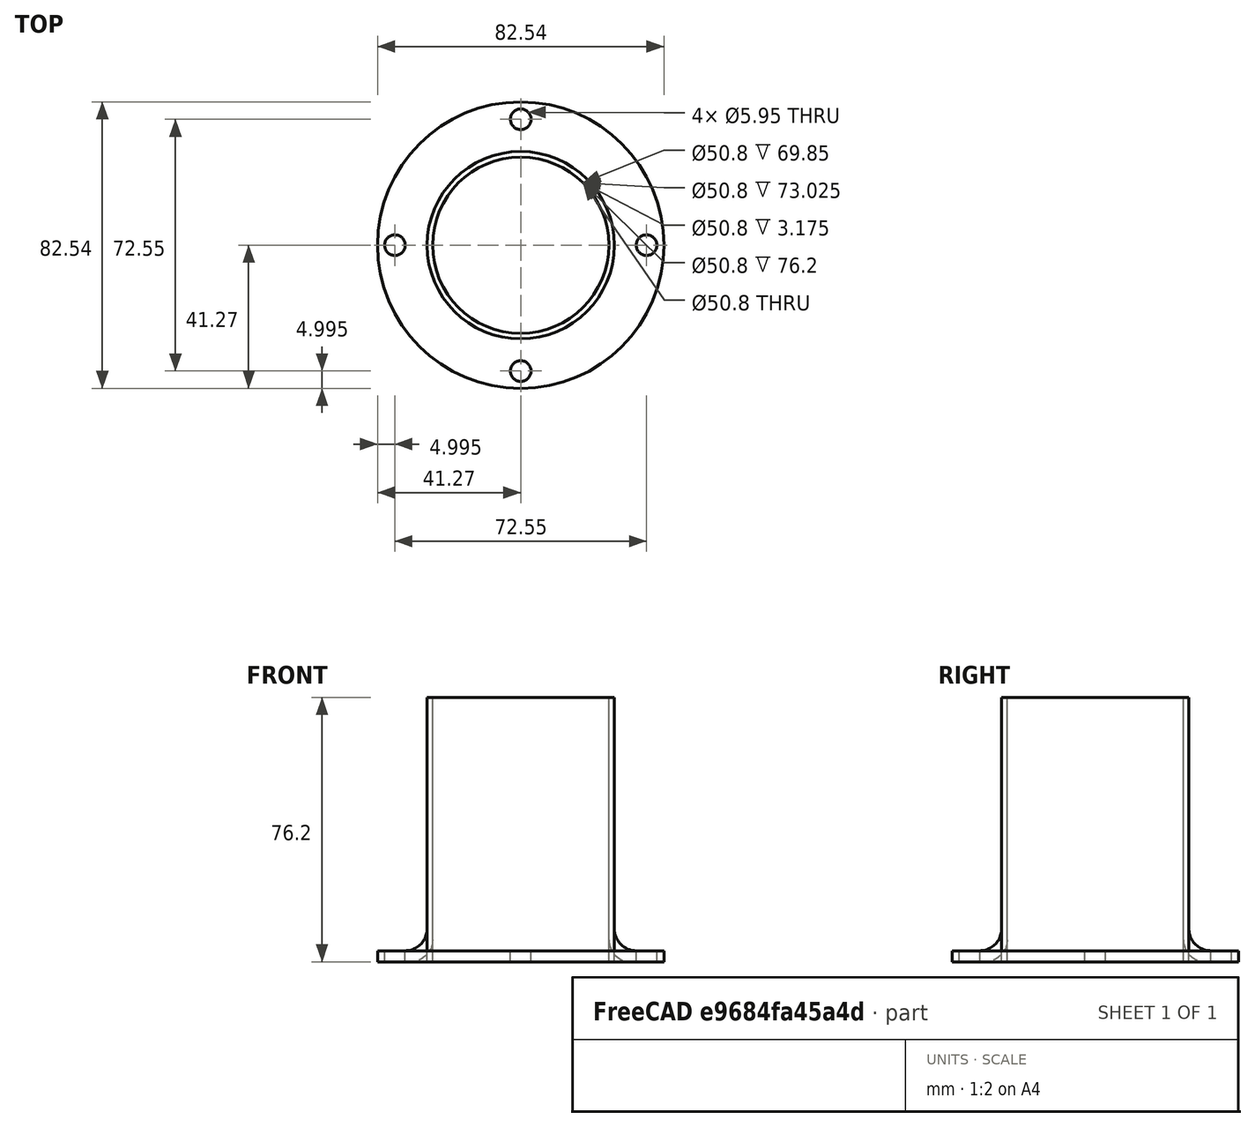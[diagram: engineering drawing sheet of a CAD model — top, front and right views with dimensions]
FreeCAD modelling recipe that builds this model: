
FCSTD DOCUMENT  (FreeCAD 0.22R38385 (Git))
Label: 2x3 Speaker Port
License: All rights reserved
objects: Part::FeaturePython×4, PartDesign::Fillet×2, Part::Fuse×1, Spreadsheet::Sheet×1, Mesh::Feature×1, PartDesign::Boolean×1, Sketcher::SketchObject×1, PartDesign::Hole×1, PartDesign::Body×1
note: 19 computed .brp shape members not serialized (recipe doc carries the construction recipe); baked Part::Feature solids carry a one-line shape summary decoded from their .brp

FEATURE [Part::FeaturePython] Tube  # WARN: FeaturePython — macro-defined, semantics opaque (R4)
  AttacherType = Attacher::AttachEngine3D
  Height = 76.2
  InnerRadius = 25.4
  OuterRadius = 26.9875
  expr: Height = Spreadsheet.port_length
  expr: InnerRadius = Spreadsheet.inner_radius
  expr: OuterRadius = Spreadsheet.outer_radius
FEATURE [Part::FeaturePython] Tube001  # WARN: FeaturePython — macro-defined, semantics opaque (R4)
  AttacherType = Attacher::AttachEngine3D
  Height = 3.175
  InnerRadius = 25.4
  OuterRadius = 41.275
  expr: Height = Spreadsheet.flange_thickness
  expr: InnerRadius = Spreadsheet.inner_radius
  expr: OuterRadius = Spreadsheet.flange_radius
FEATURE [Part::Fuse] Fusion
  Base = -> Tube
  Tool = -> Tube001
FEATURE [Spreadsheet::Sheet] Spreadsheet
  cells = A1='port_diameter; B1(port_diameter)==2 "; A2='port_length; B2(port_length)==3 "; A3='wall_thickness; B3(wall_thickness)==0.0625 "; A4='flange_diameter; B4(flange_diameter)==3.25 "; A5='flange_fillet; B5(flange_fillet)==0.25 "; A6='flange_thickness; B6(flange_thickness)==0.125 "; A7='screw_diameter; B7(screw_diameter)==5 mm; A9='computed values; A10='inner_radius; B10(inner_radius)==port_diameter / 2; A11='outer_radius; B11(outer_radius)==wall_thickness + inner_radius; A12='flange_radius; B12(flange_radius)==flange_diameter / 2; A13='screw_radius; B13(screw_radius)==2.5 mm
FEATURE [Mesh::Feature] Mesh  label="Body (Meshed)"
FEATURE [Part::FeaturePython] Tube002  # WARN: FeaturePython — macro-defined, semantics opaque (R4)
  AttacherType = Attacher::AttachEngine3D
  Height = 76.2
  InnerRadius = 25.4
  OuterRadius = 26.9875
  expr: .Placement.Base.z = 0
  expr: Height = Spreadsheet.port_length
  expr: InnerRadius = Spreadsheet.inner_radius
  expr: OuterRadius = Spreadsheet.outer_radius
FEATURE [Part::FeaturePython] Tube003  # WARN: FeaturePython — macro-defined, semantics opaque (R4)
  AttacherType = Attacher::AttachEngine3D
  Height = 3.175
  InnerRadius = 25.4
  OuterRadius = 41.275
  expr: Height = Spreadsheet.flange_thickness
  expr: InnerRadius = Spreadsheet.inner_radius
  expr: OuterRadius = Spreadsheet.flange_radius
FEATURE [PartDesign::Boolean] Boolean
  Group = -> [Tube003,Tube002]
  Refine = true
  Suppressed = false
  Type = 0
  UsePlacement = true
FEATURE [PartDesign::Fillet] Fillet
  Base = -> Boolean [Edge8]
  BaseFeature = -> Boolean
  Radius = 6.35
  SupportTransform = false
  Suppressed = false
  UseAllEdges = false
  expr: Radius = Spreadsheet.flange_fillet
FEATURE [PartDesign::Fillet] Fillet001
  Base = -> Fillet [Edge9]
  BaseFeature = -> Fillet
  Radius = 6.35
  SupportTransform = false
  Suppressed = false
  UseAllEdges = false
  expr: Radius = Spreadsheet.flange_fillet
FEATURE [Sketcher::SketchObject] Sketch
  ArcFitTolerance = 0
  AttachmentSupport = -> [Fillet001]
  FullyConstrained = true
  MakeInternals = false
  MapMode = 5
  Placement = pos=(0,0,0) rot=(1,0,0;3.14159rad)
  expr: Constraints[10] = Spreadsheet.flange_radius - Spreadsheet.screw_diameter
  expr: Constraints[11] = Spreadsheet.flange_radius - Spreadsheet.screw_diameter
  expr: Constraints[1] = Spreadsheet.flange_radius - Spreadsheet.screw_diameter
  expr: Constraints[2] = Spreadsheet.screw_radius
  expr: Constraints[6] = Spreadsheet.screw_radius
  expr: Constraints[7] = Spreadsheet.screw_radius
  expr: Constraints[8] = Spreadsheet.screw_radius
  expr: Constraints[9] = Spreadsheet.flange_radius - Spreadsheet.screw_diameter
  sketch-geometry (4):
    g0: Circle CenterX=0 CenterY=36.275 CenterZ=0 NormalX=0 NormalY=0 NormalZ=1 AngleXU=0 Radius=2.5
    g1: Circle CenterX=36.275 CenterY=0 CenterZ=0 NormalX=0 NormalY=0 NormalZ=1 AngleXU=0 Radius=2.5
    g2: Circle CenterX=0 CenterY=-36.275 CenterZ=0 NormalX=0 NormalY=0 NormalZ=1 AngleXU=0 Radius=2.5
    g3: Circle CenterX=-36.275 CenterY=0 CenterZ=0 NormalX=0 NormalY=0 NormalZ=1 AngleXU=0 Radius=2.5
  constraints (12):
    c: PointOnObject(g0,g-2)
    c: DistanceY(g-1,g0) = 36.275
    c: Radius(g0) = 2.5
    c: PointOnObject(g3,g-1)
    c: PointOnObject(g2,g-2)
    c: PointOnObject(g1,g-1)
    c: Radius(g3) = 2.5
    c: Radius(g1) = 2.5
    c: Radius(g2) = 2.5
    c: DistanceX(g3,g-1) = 36.275
    c: DistanceX(g-1,g1) = 36.275
    c: DistanceY(g2,g-1) = 36.275
FEATURE [PartDesign::Hole] Hole
  BaseFeature = -> Fillet001
  CustomThreadClearance = 0
  Depth = 25.0031
  DepthType = 0
  Diameter = 5.95312
  DrillForDepth = false
  DrillPoint = 1
  DrillPointAngle = 118
  HoleCutCountersinkAngle = 90
  HoleCutCustomValues = false
  HoleCutDepth = 0
  HoleCutDiameter = 0
  HoleCutType = 0
  ModelThread = false
  Profile = -> Sketch
  Suppressed = false
  Tapered = false
  TaperedAngle = 90
  ThreadClass = 0
  ThreadDepth = 25.0031
  ThreadDepthType = 0
  ThreadDirection = 0
  ThreadFit = 0
  ThreadSize = 0
  ThreadType = 0
  Threaded = false
  UseCustomThreadClearance = false
FEATURE [PartDesign::Body] Body  label="2x3 port"
  AllowCompound = false
  Group = -> [Boolean,Fillet,Fillet001,Sketch,Hole]
  Origin = -> Origin
  Tip = -> Hole
